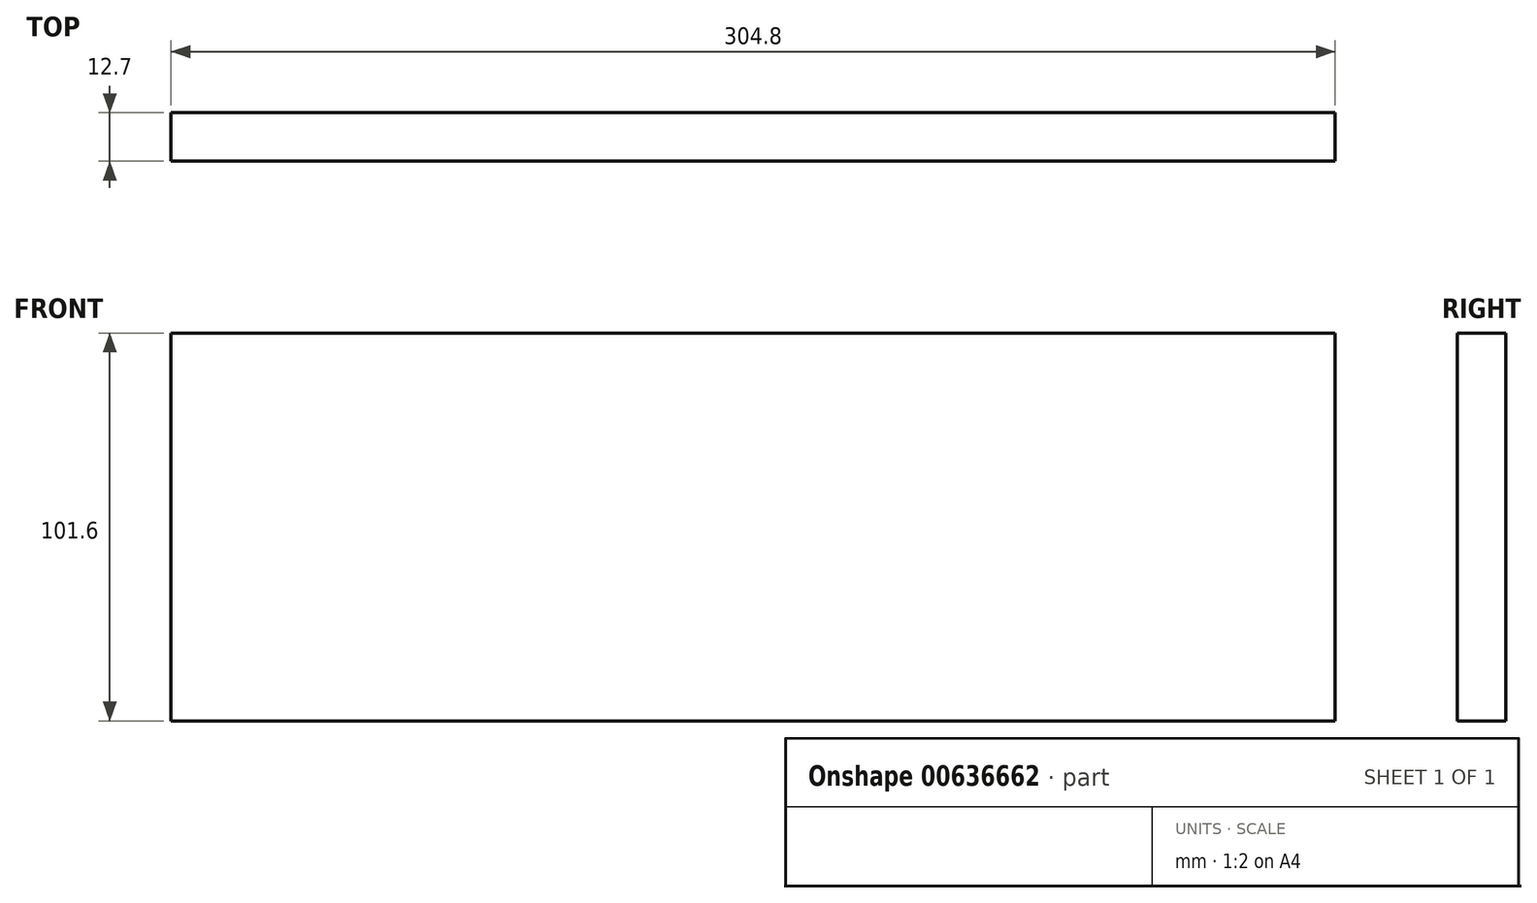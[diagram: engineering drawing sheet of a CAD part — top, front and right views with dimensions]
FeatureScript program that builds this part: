
annotation { "Feature Type Name" : "Feature", "Feature Type Description" : "" }
export const myFeature = defineFeature(function(context is Context, id is Id, definition is map)
    precondition{}
    {
        {
            var Q0;
            Q0=qCreatedBy(makeId("Front.planeOp"),FACE);
            var sketch = newSketch(context, id + "F0", { "sketchPlane" : qUnion([Q0])});
            skLineSegment(sketch, "E0.bottom", {"start": v(-55.54, 36.15) * mm, "end": v(249.26, 36.15) * mm});
            skLineSegment(sketch, "E0.top", {"start": v(-55.54, -65.45) * mm, "end": v(249.26, -65.45) * mm});
            skLineSegment(sketch, "E0.left", {"start": v(-55.54, 36.15) * mm, "end": v(-55.54, -65.45) * mm});
            skLineSegment(sketch, "E0.right", {"start": v(249.26, 36.15) * mm, "end": v(249.26, -65.45) * mm});
            skSolve(sketch);
        }
        {
            var Q0;
            Q0 = qSketchRegion(id + "F0", true);
            extrude(context, id + "F1", {"entities" : qUnion([Q0]), "depth" : 12.7 * mm, "offsetDistance" : 25.4 * mm});
        }
    });
